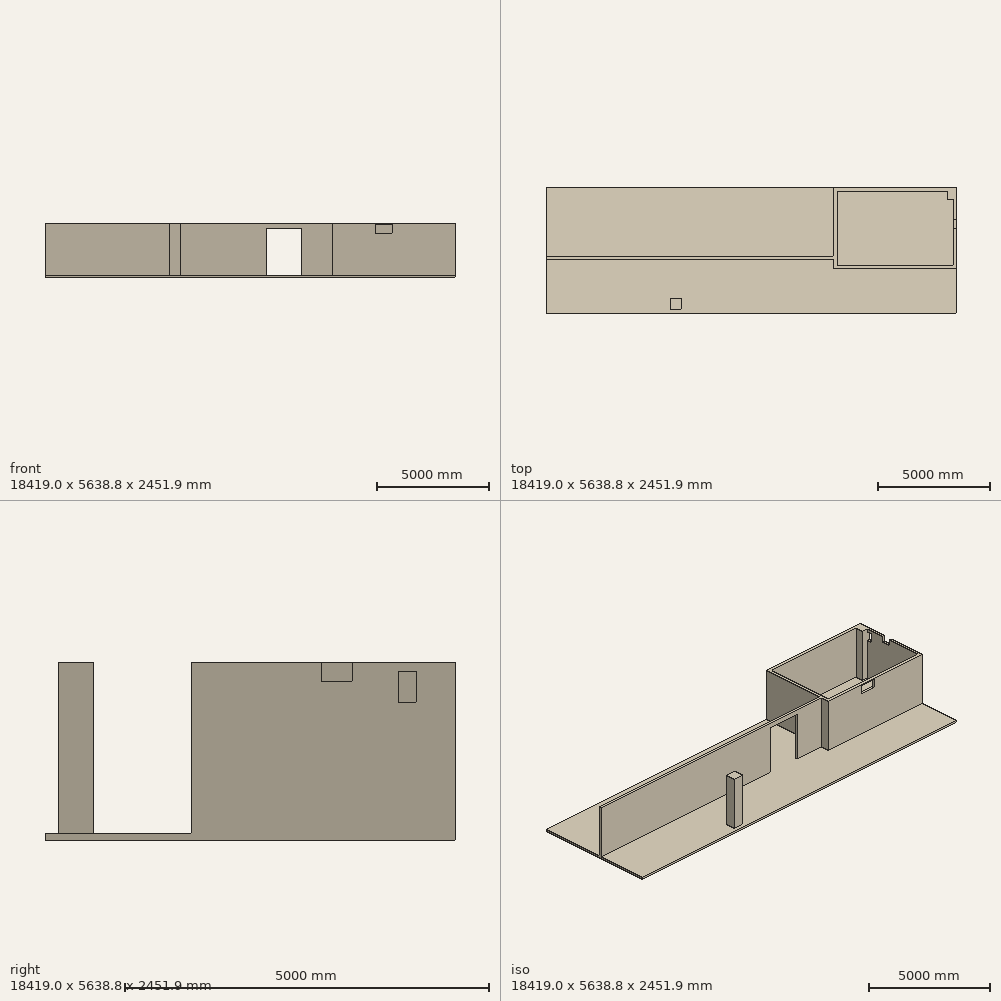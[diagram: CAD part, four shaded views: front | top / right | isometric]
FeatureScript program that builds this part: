
annotation { "Feature Type Name" : "Feature", "Feature Type Description" : "" }
export const myFeature = defineFeature(function(context is Context, id is Id, definition is map)
    precondition{}
    {
        {
            var Q0;
            Q0=qCreatedBy(makeId("Top.planeOp"),FACE);
            var sketch = newSketch(context, id + "F0", { "sketchPlane" : qUnion([Q0])});
            skLineSegment(sketch, "E0.bottom", {"start": v(0, 0) * mm, "end": v(18288, 0) * mm});
            skLineSegment(sketch, "E0.top", {"start": v(0, 5486.4) * mm, "end": v(18288, 5486.4) * mm});
            skLineSegment(sketch, "E0.left", {"start": v(0, 0) * mm, "end": v(0, 5486.4) * mm});
            skLineSegment(sketch, "E0.right", {"start": v(18288, 0) * mm, "end": v(18288, 5486.4) * mm});
            skSolve(sketch);
        }
        {
            var Q0;
            Q0=makeQuery(id+"F0.imprint","IMPRINT",FACE,{"disambiguationData":[TD([[makeQuery(id+"F0.imprint","IMPRINT",EDGE,{"derivedFrom":sQuery(id+"F0.wireOp",EDGE,"E0.bottom")}),1.0]])]});
            extrude(context, id + "F1", {"entities" : qUnion([Q0]), "depth" : 101.6 * mm});
        }
        {
            var Q0;
            Q0=makeQuery(id+"F1.opExtrude","CAP_FACE",FACE,{"disambiguationData":[OSD([sQuery(id+"F0.wireOp",EDGE,"E0.bottom"),sQuery(id+"F0.wireOp",EDGE,"E0.top"),sQuery(id+"F0.wireOp",EDGE,"E0.left"),sQuery(id+"F0.wireOp",EDGE,"E0.right")])],"isStart":false});
            var sketch = newSketch(context, id + "F2", { "sketchPlane" : qUnion([Q0])});
            skLineSegment(sketch, "E1.bottom", {"start": v(18288, 5486.4) * mm, "end": v(13335, 5486.4) * mm, "construction": true});
            skLineSegment(sketch, "E1.top", {"start": v(18288, 2128.84) * mm, "end": v(13335, 2128.84) * mm, "construction": true});
            skLineSegment(sketch, "E1.left", {"start": v(18288, 5486.4) * mm, "end": v(18288, 2128.84) * mm, "construction": true});
            skLineSegment(sketch, "E1.right", {"start": v(13335, 5486.4) * mm, "end": v(13335, 2128.84) * mm, "construction": true});
            skLineSegment(sketch, "E2.bottom", {"start": v(18288, 2128.84) * mm, "end": v(13335, 2128.84) * mm});
            skLineSegment(sketch, "E2.top", {"start": v(18288, 1976.44) * mm, "end": v(13335, 1976.44) * mm});
            skLineSegment(sketch, "E2.left", {"start": v(18288, 2128.84) * mm, "end": v(18288, 1976.44) * mm});
            skLineSegment(sketch, "E2.right", {"start": v(13335, 2128.84) * mm, "end": v(13335, 1976.44) * mm});
            skLineSegment(sketch, "E3.bottom", {"start": v(13335, 5486.4) * mm, "end": v(13182.6, 5486.4) * mm});
            skLineSegment(sketch, "E3.top", {"start": v(13335, 2128.84) * mm, "end": v(13182.6, 2128.84) * mm});
            skLineSegment(sketch, "E3.left", {"start": v(13335, 5486.4) * mm, "end": v(13335, 2128.84) * mm});
            skLineSegment(sketch, "E3.right", {"start": v(13182.6, 5486.4) * mm, "end": v(13182.6, 2128.84) * mm});
            skLineSegment(sketch, "E4.bottom", {"start": v(13335, 1976.44) * mm, "end": v(13182.6, 1976.44) * mm});
            skLineSegment(sketch, "E4.left", {"start": v(13335, 1976.44) * mm, "end": v(13335, 2128.84) * mm});
            skLineSegment(sketch, "E4.right", {"start": v(13182.6, 1976.44) * mm, "end": v(13182.6, 2128.84) * mm});
            skSolve(sketch);
        }
        {
            var Q0;
            Q0=makeQuery(id+"F2.imprint","IMPRINT",FACE,{"disambiguationData":[TD([[makeQuery(id+"F2.imprint","IMPRINT",EDGE,{"derivedFrom":sQuery(id+"F2.wireOp",EDGE,"E2.bottom")}),1.0]])]});
            var Q1;
            Q1=makeQuery(id+"F2.imprint","IMPRINT",FACE,{"disambiguationData":[TD([[makeQuery(id+"F2.imprint","IMPRINT",EDGE,{"derivedFrom":sQuery(id+"F2.wireOp",EDGE,"E3.bottom")}),-1.0]])]});
            var Q2;
            Q2=makeQuery(id+"F2.imprint","IMPRINT",FACE,{"disambiguationData":[TD([[makeQuery(id+"F2.imprint","IMPRINT",EDGE,{"derivedFrom":sQuery(id+"F2.wireOp",EDGE,"E4.bottom")}),-1.0]])]});
            extrude(context, id + "F3", {"entities" : qUnion([Q0, Q1, Q2]), "operationType" : NewBodyOperationType.ADD, "depth" : 2426.5 * mm});
        }
        {
            var Q0;
            Q0=makeQuery(id+"F3.boolean.opBoolean","MERGE",FACE,{"derivedFrom":[makeQuery(id+"F1.opExtrude","SWEPT_FACE",FACE,{"disambiguationData":[OSD([sQuery(id+"F0.wireOp",EDGE,"E0.right")])]}),makeQuery(id+"F3.opExtrude","SWEPT_FACE",FACE,{"disambiguationData":[OSD([sQuery(id+"F2.wireOp",EDGE,"E2.left")])]})]});
            extrude(context, id + "F4", {"entities" : qUnion([Q0]), "operationType" : NewBodyOperationType.ADD, "depth" : 152.4 * mm});
        }
        {
            var Q0;
            {var subQ0=sQuery(id+"F0.wireOp",EDGE,"E0.top");Q0=makeQuery(id+"F4.boolean.opBoolean","MERGE",FACE,{"derivedFrom":[makeQuery(id+"F3.boolean.opBoolean","MERGE",FACE,{"derivedFrom":[makeQuery(id+"F1.opExtrude","SWEPT_FACE",FACE,{"disambiguationData":[OSD([subQ0])]}),makeQuery(id+"F3.opExtrude","SWEPT_FACE",FACE,{"disambiguationData":[OSD([sQuery(id+"F2.wireOp",EDGE,"E3.bottom")])]})]}),makeQuery(id+"F4.opExtrude","SWEPT_FACE",FACE,{"disambiguationData":[OSD([subQ0,sQuery(id+"F0.wireOp",EDGE,"E0.right")])]})]});}
            extrude(context, id + "F5", {"entities" : qUnion([Q0]), "operationType" : NewBodyOperationType.ADD, "depth" : 152.4 * mm});
        }
        {
            var Q0;
            {var subQ0=sQuery(id+"F0.wireOp",EDGE,"E0.right");var subQ1=sQuery(id+"F0.wireOp",EDGE,"E0.top");var subQ3=makeQuery(id+"F1.opExtrude","SWEPT_FACE",FACE,{"disambiguationData":[OSD([subQ0])]});var subQ4=makeQuery(id+"F1.opExtrude","SWEPT_FACE",FACE,{"disambiguationData":[OSD([subQ1])]});var subQ5=makeQuery(id+"F1.opExtrude","CAP_FACE",FACE,{"disambiguationData":[OSD([sQuery(id+"F0.wireOp",EDGE,"E0.bottom"),subQ1,sQuery(id+"F0.wireOp",EDGE,"E0.left"),subQ0])],"isStart":false});var subQ8=makeQuery(id+"F3.opExtrude","SWEPT_FACE",FACE,{"disambiguationData":[OSD([sQuery(id+"F2.wireOp",EDGE,"E2.bottom")])]});Q0=makeQuery(id+"F5.boolean.opBoolean","MERGE",FACE,{"derivedFrom":[makeQuery(id+"F4.boolean.opBoolean","MERGE",FACE,{"derivedFrom":[makeQuery(id+"F3.boolean.opBoolean","SPLIT",FACE,{"disambiguationData":[TD([subQ8])],"derivedFrom":subQ5}),makeQuery(id+"F4.opExtrude","SWEPT_FACE",FACE,{"disambiguationData":[OSD([subQ0]),TDD([makeQuery(id+"F3.boolean.opBoolean","SPLIT",EDGE,{"disambiguationData":[TD([subQ4])],"derivedFrom":makeQuery(id+"F1.opExtrude","CAP_EDGE",EDGE,{"disambiguationData":[OSD([subQ0])],"isStart":false})})])]})]}),makeQuery(id+"F5.opExtrude","SWEPT_FACE",FACE,{"disambiguationData":[OSD([subQ1,subQ0]),TDD([makeQuery(id+"F4.boolean.opBoolean","MERGE",EDGE,{"derivedFrom":[makeQuery(id+"F3.boolean.opBoolean","SPLIT",EDGE,{"disambiguationData":[TD([subQ3])],"derivedFrom":makeQuery(id+"F1.opExtrude","CAP_EDGE",EDGE,{"disambiguationData":[OSD([subQ1])],"isStart":false})}),makeQuery(id+"F4.opExtrude","SWEPT_EDGE",EDGE,{"disambiguationData":[OSD([subQ1,subQ0]),TDD([makeQuery(id+"F1.opExtrude","CAP_VERTEX",VERTEX,{"disambiguationData":[OSD([subQ1,subQ0])],"isStart":false})])]})]})])]})]});}
            var sketch = newSketch(context, id + "F6", { "sketchPlane" : qUnion([Q0])});
            skLineSegment(sketch, "E5.bottom", {"start": v(18440.4, 2128.84) * mm, "end": v(18288, 2128.84) * mm});
            skLineSegment(sketch, "E5.top", {"start": v(18440.4, 5638.8) * mm, "end": v(18288, 5638.8) * mm});
            skLineSegment(sketch, "E5.left", {"start": v(18440.4, 2128.84) * mm, "end": v(18440.4, 5638.8) * mm});
            skLineSegment(sketch, "E5.right", {"start": v(18288, 2128.84) * mm, "end": v(18288, 5638.8) * mm});
            skLineSegment(sketch, "E6.bottom", {"start": v(13335, 5638.8) * mm, "end": v(18288, 5638.8) * mm});
            skLineSegment(sketch, "E6.top", {"start": v(13335, 5486.4) * mm, "end": v(18288, 5486.4) * mm});
            skLineSegment(sketch, "E6.left", {"start": v(13335, 5638.8) * mm, "end": v(13335, 5486.4) * mm});
            skLineSegment(sketch, "E6.right", {"start": v(18288, 5638.8) * mm, "end": v(18288, 5486.4) * mm});
            skSolve(sketch);
        }
        {
            var Q0;
            Q0=makeQuery(id+"F6.imprint","IMPRINT",FACE,{"disambiguationData":[TD([[makeQuery(id+"F6.imprint","IMPRINT",EDGE,{"derivedFrom":sQuery(id+"F6.wireOp",EDGE,"E6.bottom")}),-1.0]])]});
            var Q1;
            Q1=makeQuery(id+"F6.imprint","IMPRINT",FACE,{"disambiguationData":[TD([[makeQuery(id+"F6.imprint","IMPRINT",EDGE,{"derivedFrom":sQuery(id+"F6.wireOp",EDGE,"E5.bottom")}),-1.0]])]});
            extrude(context, id + "F7", {"entities" : qUnion([Q0, Q1]), "operationType" : NewBodyOperationType.ADD, "depth" : 2350.3 * mm});
        }
        {
            var Q0;
            {var subQ0=sQuery(id+"F2.wireOp",EDGE,"E3.bottom");var subQ1=sQuery(id+"F2.wireOp",EDGE,"E2.left");Q0=makeQuery(id+"F5.boolean.opBoolean","MERGE",FACE,{"derivedFrom":[makeQuery(id+"F4.boolean.opBoolean","MERGE",FACE,{"derivedFrom":[makeQuery(id+"F3.opExtrude","CAP_FACE",FACE,{"disambiguationData":[OSD([sQuery(id+"F2.wireOp",EDGE,"E2.bottom"),sQuery(id+"F2.wireOp",EDGE,"E2.top"),subQ1,subQ0,sQuery(id+"F2.wireOp",EDGE,"E3.left"),sQuery(id+"F2.wireOp",EDGE,"E3.right"),sQuery(id+"F2.wireOp",EDGE,"E4.bottom"),sQuery(id+"F2.wireOp",EDGE,"E4.right")])],"isStart":false}),makeQuery(id+"F4.opExtrude","SWEPT_FACE",FACE,{"disambiguationData":[OSD([subQ1])]})]}),makeQuery(id+"F5.opExtrude","SWEPT_FACE",FACE,{"disambiguationData":[OSD([subQ0])]})]});}
            extrude(context, id + "F8", {"entities" : qUnion([Q0]), "operationType" : NewBodyOperationType.REMOVE, "oppositeDirection" : true, "depth" : 76.2 * mm});
        }
        {
            var Q0;
            {var subQ0=sQuery(id+"F0.wireOp",EDGE,"E0.right");var subQ1=sQuery(id+"F0.wireOp",EDGE,"E0.top");var subQ3=makeQuery(id+"F1.opExtrude","SWEPT_FACE",FACE,{"disambiguationData":[OSD([subQ0])]});var subQ4=makeQuery(id+"F1.opExtrude","SWEPT_FACE",FACE,{"disambiguationData":[OSD([subQ1])]});var subQ5=makeQuery(id+"F1.opExtrude","CAP_FACE",FACE,{"disambiguationData":[OSD([sQuery(id+"F0.wireOp",EDGE,"E0.bottom"),subQ1,sQuery(id+"F0.wireOp",EDGE,"E0.left"),subQ0])],"isStart":false});var subQ8=makeQuery(id+"F3.opExtrude","SWEPT_FACE",FACE,{"disambiguationData":[OSD([sQuery(id+"F2.wireOp",EDGE,"E2.bottom")])]});Q0=makeQuery(id+"F5.boolean.opBoolean","MERGE",FACE,{"derivedFrom":[makeQuery(id+"F4.boolean.opBoolean","MERGE",FACE,{"derivedFrom":[makeQuery(id+"F3.boolean.opBoolean","SPLIT",FACE,{"disambiguationData":[TD([subQ8])],"derivedFrom":subQ5}),makeQuery(id+"F4.opExtrude","SWEPT_FACE",FACE,{"disambiguationData":[OSD([subQ0]),TDD([makeQuery(id+"F3.boolean.opBoolean","SPLIT",EDGE,{"disambiguationData":[TD([subQ4])],"derivedFrom":makeQuery(id+"F1.opExtrude","CAP_EDGE",EDGE,{"disambiguationData":[OSD([subQ0])],"isStart":false})})])]})]}),makeQuery(id+"F5.opExtrude","SWEPT_FACE",FACE,{"disambiguationData":[OSD([subQ1,subQ0]),TDD([makeQuery(id+"F4.boolean.opBoolean","MERGE",EDGE,{"derivedFrom":[makeQuery(id+"F3.boolean.opBoolean","SPLIT",EDGE,{"disambiguationData":[TD([subQ3])],"derivedFrom":makeQuery(id+"F1.opExtrude","CAP_EDGE",EDGE,{"disambiguationData":[OSD([subQ1])],"isStart":false})}),makeQuery(id+"F4.opExtrude","SWEPT_EDGE",EDGE,{"disambiguationData":[OSD([subQ1,subQ0]),TDD([makeQuery(id+"F1.opExtrude","CAP_VERTEX",VERTEX,{"disambiguationData":[OSD([subQ1,subQ0])],"isStart":false})])]})]})])]})]});}
            var sketch = newSketch(context, id + "F9", { "sketchPlane" : qUnion([Q0])});
            skLineSegment(sketch, "E7.bottom", {"start": v(18288, 5486.4) * mm, "end": v(17907, 5486.4) * mm});
            skLineSegment(sketch, "E7.top", {"start": v(18288, 5207) * mm, "end": v(17907, 5207) * mm});
            skLineSegment(sketch, "E7.left", {"start": v(18288, 5486.4) * mm, "end": v(18288, 5207) * mm});
            skLineSegment(sketch, "E7.right", {"start": v(17907, 5486.4) * mm, "end": v(17907, 5207) * mm});
            skSolve(sketch);
        }
        {
            var Q0;
            Q0=makeQuery(id+"F9.imprint","IMPRINT",FACE,{"disambiguationData":[TD([[makeQuery(id+"F9.imprint","IMPRINT",EDGE,{"derivedFrom":sQuery(id+"F9.wireOp",EDGE,"E7.bottom")}),-1.0]])]});
            var Q1;
            Q1=makeQuery(id+"F8.boolean.opBoolean","MERGE",FACE,{"derivedFrom":[makeQuery(id+"F7.opExtrude","CAP_FACE",FACE,{"disambiguationData":[OSD([sQuery(id+"F6.wireOp",EDGE,"E5.bottom"),sQuery(id+"F6.wireOp",EDGE,"E5.top"),sQuery(id+"F6.wireOp",EDGE,"E5.left"),sQuery(id+"F6.wireOp",EDGE,"E5.right"),sQuery(id+"F6.wireOp",EDGE,"E6.bottom"),sQuery(id+"F6.wireOp",EDGE,"E6.top"),sQuery(id+"F6.wireOp",EDGE,"E6.left")])],"isStart":false}),makeQuery(id+"F8.opExtrude","CAP_FACE",FACE,{"disambiguationData":[OSD([sQuery(id+"F2.wireOp",EDGE,"E2.bottom"),sQuery(id+"F2.wireOp",EDGE,"E2.top"),sQuery(id+"F2.wireOp",EDGE,"E2.left"),sQuery(id+"F2.wireOp",EDGE,"E3.bottom"),sQuery(id+"F2.wireOp",EDGE,"E3.left"),sQuery(id+"F2.wireOp",EDGE,"E3.right"),sQuery(id+"F2.wireOp",EDGE,"E4.bottom"),sQuery(id+"F2.wireOp",EDGE,"E4.right")])],"isStart":false})]});
            extrude(context, id + "F10", {"entities" : qUnion([Q0]), "operationType" : NewBodyOperationType.ADD, "endBound" : BoundingType.UP_TO_SURFACE, "endBoundEntityFace" : qUnion([Q1]), "depth" : 25.4 * mm});
        }
        {
            var Q0;
            Q0=makeQuery(id+"F10.opExtrude","SWEPT_FACE",FACE,{"disambiguationData":[OSD([sQuery(id+"F9.wireOp",EDGE,"E7.top")])]});
            extrude(context, id + "F11", {"entities" : qUnion([Q0]), "operationType" : NewBodyOperationType.ADD, "depth" : 101.6 * mm});
        }
        {
            var Q0;
            {var subQ0=sQuery(id+"F9.wireOp",EDGE,"E7.right");Q0=makeQuery(id+"F11.boolean.opBoolean","MERGE",FACE,{"derivedFrom":[makeQuery(id+"F10.opExtrude","SWEPT_FACE",FACE,{"disambiguationData":[OSD([subQ0])]}),makeQuery(id+"F11.opExtrude","SWEPT_FACE",FACE,{"disambiguationData":[OSD([sQuery(id+"F9.wireOp",EDGE,"E7.top"),subQ0])]})]});}
            extrude(context, id + "F12", {"entities" : qUnion([Q0]), "operationType" : NewBodyOperationType.REMOVE, "oppositeDirection" : true, "depth" : 101.6 * mm});
        }
        {
            var Q0;
            {var subQ0=sQuery(id+"F2.wireOp",EDGE,"E3.right");Q0=makeQuery(id+"F5.boolean.opBoolean","MERGE",FACE,{"derivedFrom":[makeQuery(id+"F3.opExtrude","SWEPT_FACE",FACE,{"disambiguationData":[OSD([subQ0,sQuery(id+"F2.wireOp",EDGE,"E4.right")])]}),makeQuery(id+"F5.opExtrude","SWEPT_FACE",FACE,{"disambiguationData":[OSD([sQuery(id+"F0.wireOp",EDGE,"E0.top"),sQuery(id+"F2.wireOp",EDGE,"E3.bottom"),subQ0])]})]});}
            extrude(context, id + "F13", {"entities" : qUnion([Q0]), "operationType" : NewBodyOperationType.ADD, "depth" : 275.43 * mm});
        }
        {
            var Q0;
            {var subQ0=sQuery(id+"F2.wireOp",EDGE,"E3.left");Q0=makeQuery(id+"F5.boolean.opBoolean","MERGE",FACE,{"derivedFrom":[makeQuery(id+"F3.opExtrude","SWEPT_FACE",FACE,{"disambiguationData":[OSD([subQ0])]}),makeQuery(id+"F5.opExtrude","SWEPT_FACE",FACE,{"disambiguationData":[OSD([sQuery(id+"F0.wireOp",EDGE,"E0.top"),sQuery(id+"F2.wireOp",EDGE,"E3.bottom"),subQ0])]})]});}
            extrude(context, id + "F14", {"entities" : qUnion([Q0]), "operationType" : NewBodyOperationType.REMOVE, "oppositeDirection" : true, "depth" : 275.43 * mm});
        }
        {
            var Q0;
            {var subQ0=sQuery(id+"F2.wireOp",EDGE,"E4.bottom");var subQ1=sQuery(id+"F2.wireOp",EDGE,"E2.top");Q0=makeQuery(id+"F13.boolean.opBoolean","MERGE",FACE,{"derivedFrom":[makeQuery(id+"F4.boolean.opBoolean","MERGE",FACE,{"derivedFrom":[makeQuery(id+"F3.opExtrude","SWEPT_FACE",FACE,{"disambiguationData":[OSD([subQ1,subQ0])]}),makeQuery(id+"F4.opExtrude","SWEPT_FACE",FACE,{"disambiguationData":[OSD([sQuery(id+"F0.wireOp",EDGE,"E0.right"),subQ1,sQuery(id+"F2.wireOp",EDGE,"E2.left")])]})]}),makeQuery(id+"F13.opExtrude","SWEPT_FACE",FACE,{"disambiguationData":[OSD([subQ0,sQuery(id+"F2.wireOp",EDGE,"E4.right")])]})]});}
            extrude(context, id + "F15", {"entities" : qUnion([Q0]), "operationType" : NewBodyOperationType.REMOVE, "oppositeDirection" : true, "depth" : 25.4 * mm});
        }
        {
            var Q0;
            {var subQ0=sQuery(id+"F2.wireOp",EDGE,"E2.bottom");Q0=makeQuery(id+"F14.boolean.opBoolean","MERGE",FACE,{"derivedFrom":[makeQuery(id+"F4.boolean.opBoolean","MERGE",FACE,{"derivedFrom":[makeQuery(id+"F3.opExtrude","SWEPT_FACE",FACE,{"disambiguationData":[OSD([subQ0])]}),makeQuery(id+"F4.opExtrude","SWEPT_FACE",FACE,{"disambiguationData":[OSD([sQuery(id+"F0.wireOp",EDGE,"E0.right"),subQ0,sQuery(id+"F2.wireOp",EDGE,"E2.left")])]})]}),makeQuery(id+"F14.opExtrude","SWEPT_FACE",FACE,{"disambiguationData":[OSD([subQ0,sQuery(id+"F2.wireOp",EDGE,"E3.left"),sQuery(id+"F2.wireOp",EDGE,"E3.top"),sQuery(id+"F2.wireOp",EDGE,"E4.left")])]})]});}
            var sketch = newSketch(context, id + "F16", { "sketchPlane" : qUnion([Q0])});
            skLineSegment(sketch, "E8.bottom", {"start": v(-13059.57, 2451.9) * mm, "end": v(-14431.17, 2451.9) * mm, "construction": true});
            skLineSegment(sketch, "E8.top", {"start": v(-13059.57, 2197.9) * mm, "end": v(-14431.17, 2197.9) * mm, "construction": true});
            skLineSegment(sketch, "E8.left", {"start": v(-13059.57, 2451.9) * mm, "end": v(-13059.57, 2197.9) * mm, "construction": true});
            skLineSegment(sketch, "E8.right", {"start": v(-14431.17, 2451.9) * mm, "end": v(-14431.17, 2197.9) * mm, "construction": true});
            skLineSegment(sketch, "E9.bottom", {"start": v(-14431.17, 2197.9) * mm, "end": v(-15193.17, 2197.9) * mm});
            skLineSegment(sketch, "E9.top", {"start": v(-14431.17, 1943.9) * mm, "end": v(-15193.17, 1943.9) * mm});
            skLineSegment(sketch, "E9.left", {"start": v(-14431.17, 2197.9) * mm, "end": v(-14431.17, 1943.9) * mm});
            skLineSegment(sketch, "E9.right", {"start": v(-15193.17, 2197.9) * mm, "end": v(-15193.17, 1943.9) * mm});
            skSolve(sketch);
        }
        {
            var Q0;
            Q0=makeQuery(id+"F16.imprint","IMPRINT",FACE,{"disambiguationData":[TD([[makeQuery(id+"F16.imprint","IMPRINT",EDGE,{"derivedFrom":sQuery(id+"F16.wireOp",EDGE,"E9.bottom")}),1.0]])]});
            extrude(context, id + "F17", {"entities" : qUnion([Q0]), "operationType" : NewBodyOperationType.REMOVE, "endBound" : BoundingType.THROUGH_ALL, "oppositeDirection" : true, "depth" : 25.4 * mm});
        }
        {
            var Q0;
            Q0=makeQuery(id+"F17.boolean.opBoolean","COPY",FACE,{"derivedFrom":makeQuery(id+"F17.opExtrude","SWEPT_FACE",FACE,{"disambiguationData":[OSD([sQuery(id+"F16.wireOp",EDGE,"E9.bottom")])]})});
            extrude(context, id + "F18", {"entities" : qUnion([Q0]), "operationType" : NewBodyOperationType.REMOVE, "oppositeDirection" : true, "depth" : 190.5 * mm});
        }
        {
            var Q0;
            Q0=makeQuery(id+"F17.boolean.opBoolean","COPY",FACE,{"derivedFrom":makeQuery(id+"F17.opExtrude","SWEPT_FACE",FACE,{"disambiguationData":[OSD([sQuery(id+"F16.wireOp",EDGE,"E9.top")])]})});
            extrude(context, id + "F19", {"entities" : qUnion([Q0]), "operationType" : NewBodyOperationType.ADD, "depth" : 63.5 * mm});
        }
        {
            var Q0;
            Q0=makeQuery(id+"F7.opExtrude","SWEPT_FACE",FACE,{"disambiguationData":[OSD([sQuery(id+"F6.wireOp",EDGE,"E5.right")])]});
            var sketch = newSketch(context, id + "F20", { "sketchPlane" : qUnion([Q0])});
            skLineSegment(sketch, "E10.bottom", {"start": v(-5105.4, 2451.9) * mm, "end": v(-4851.4, 2451.9) * mm, "construction": true});
            skLineSegment(sketch, "E10.top", {"start": v(-5105.4, 2375.7) * mm, "end": v(-4851.4, 2375.7) * mm, "construction": true});
            skLineSegment(sketch, "E10.left", {"start": v(-5105.4, 2451.9) * mm, "end": v(-5105.4, 2375.7) * mm, "construction": true});
            skLineSegment(sketch, "E10.right", {"start": v(-4851.4, 2451.9) * mm, "end": v(-4851.4, 2375.7) * mm, "construction": true});
            skLineSegment(sketch, "E11.bottom", {"start": v(-4851.4, 2375.7) * mm, "end": v(-5105.4, 2375.7) * mm});
            skLineSegment(sketch, "E11.top", {"start": v(-4851.4, 2070.9) * mm, "end": v(-5105.4, 2070.9) * mm});
            skLineSegment(sketch, "E11.left", {"start": v(-4851.4, 2375.7) * mm, "end": v(-4851.4, 2070.9) * mm});
            skLineSegment(sketch, "E11.right", {"start": v(-5105.4, 2375.7) * mm, "end": v(-5105.4, 2070.9) * mm});
            skSolve(sketch);
        }
        {
            var Q0;
            Q0=makeQuery(id+"F20.imprint","IMPRINT",FACE,{"disambiguationData":[TD([[makeQuery(id+"F20.imprint","IMPRINT",EDGE,{"derivedFrom":sQuery(id+"F20.wireOp",EDGE,"E11.bottom")}),1.0]])]});
            extrude(context, id + "F21", {"entities" : qUnion([Q0]), "operationType" : NewBodyOperationType.REMOVE, "endBound" : BoundingType.THROUGH_ALL, "oppositeDirection" : true, "depth" : 25.4 * mm});
        }
        {
            var Q0;
            Q0=makeQuery(id+"F7.opExtrude","SWEPT_FACE",FACE,{"disambiguationData":[OSD([sQuery(id+"F6.wireOp",EDGE,"E5.right")])]});
            var sketch = newSketch(context, id + "F22", { "sketchPlane" : qUnion([Q0])});
            skLineSegment(sketch, "E12.bottom", {"start": v(-4851.4, 2375.7) * mm, "end": v(-3606.8, 2375.7) * mm, "construction": true});
            skLineSegment(sketch, "E12.top", {"start": v(-4851.4, 2070.9) * mm, "end": v(-3606.8, 2070.9) * mm, "construction": true});
            skLineSegment(sketch, "E12.left", {"start": v(-4851.4, 2375.7) * mm, "end": v(-4851.4, 2070.9) * mm, "construction": true});
            skLineSegment(sketch, "E12.right", {"start": v(-3606.8, 2375.7) * mm, "end": v(-3606.8, 2070.9) * mm, "construction": true});
            skLineSegment(sketch, "E13.bottom", {"start": v(-3606.8, 2375.7) * mm, "end": v(-3888.54, 2375.7) * mm});
            skLineSegment(sketch, "E13.top", {"start": v(-3606.8, 2070.9) * mm, "end": v(-3888.54, 2070.9) * mm});
            skLineSegment(sketch, "E13.left", {"start": v(-3606.8, 2375.7) * mm, "end": v(-3606.8, 2070.9) * mm});
            skLineSegment(sketch, "E13.right", {"start": v(-3888.54, 2375.7) * mm, "end": v(-3888.54, 2070.9) * mm});
            skSolve(sketch);
        }
        {
            var Q0;
            Q0=makeQuery(id+"F22.imprint","IMPRINT",FACE,{"disambiguationData":[TD([[makeQuery(id+"F22.imprint","IMPRINT",EDGE,{"derivedFrom":sQuery(id+"F22.wireOp",EDGE,"E13.bottom")}),1.0]])]});
            extrude(context, id + "F23", {"entities" : qUnion([Q0]), "operationType" : NewBodyOperationType.REMOVE, "endBound" : BoundingType.THROUGH_ALL, "oppositeDirection" : true, "depth" : 25.4 * mm});
        }
        {
            var Q0;
            Q0=makeQuery(id+"F23.boolean.opBoolean","COPY",FACE,{"derivedFrom":makeQuery(id+"F23.opExtrude","SWEPT_FACE",FACE,{"disambiguationData":[OSD([sQuery(id+"F22.wireOp",EDGE,"E13.right")])]})});
            extrude(context, id + "F24", {"entities" : qUnion([Q0]), "operationType" : NewBodyOperationType.REMOVE, "oppositeDirection" : true, "depth" : 304.8 * mm});
        }
        {
            var Q0;
            Q0=makeQuery(id+"F23.boolean.opBoolean","COPY",FACE,{"derivedFrom":makeQuery(id+"F23.opExtrude","SWEPT_FACE",FACE,{"disambiguationData":[OSD([sQuery(id+"F22.wireOp",EDGE,"E13.left")])]})});
            extrude(context, id + "F25", {"entities" : qUnion([Q0]), "operationType" : NewBodyOperationType.ADD, "depth" : 304.8 * mm});
        }
        {
            var Q0;
            Q0=makeQuery(id+"F24.boolean.opBoolean","COPY",FACE,{"derivedFrom":makeQuery(id+"F24.opExtrude","CAP_FACE",FACE,{"disambiguationData":[OSD([sQuery(id+"F22.wireOp",EDGE,"E13.right")])],"isStart":false})});
            extrude(context, id + "F26", {"entities" : qUnion([Q0]), "operationType" : NewBodyOperationType.ADD, "depth" : 25.4 * mm});
        }
        {
            var Q0;
            Q0=makeQuery(id+"F25.opExtrude","CAP_FACE",FACE,{"disambiguationData":[OSD([sQuery(id+"F22.wireOp",EDGE,"E13.left")])],"isStart":false});
            extrude(context, id + "F27", {"entities" : qUnion([Q0]), "operationType" : NewBodyOperationType.REMOVE, "oppositeDirection" : true, "depth" : 25.4 * mm});
        }
        {
            var Q0;
            Q0=makeQuery(id+"F27.boolean.opBoolean","COPY",FACE,{"derivedFrom":makeQuery(id+"F27.opExtrude","CAP_FACE",FACE,{"disambiguationData":[OSD([sQuery(id+"F22.wireOp",EDGE,"E13.left")])],"isStart":false})});
            extrude(context, id + "F28", {"entities" : qUnion([Q0]), "operationType" : NewBodyOperationType.REMOVE, "oppositeDirection" : true, "depth" : 12.7 * mm});
        }
        {
            var Q0;
            Q0=makeQuery(id+"F26.opExtrude","CAP_FACE",FACE,{"disambiguationData":[OSD([sQuery(id+"F22.wireOp",EDGE,"E13.right")])],"isStart":false});
            extrude(context, id + "F29", {"entities" : qUnion([Q0]), "operationType" : NewBodyOperationType.ADD, "depth" : 12.7 * mm});
        }
        {
            var Q0;
            Q0=makeQuery(id+"F13.opExtrude","CAP_FACE",FACE,{"disambiguationData":[OSD([sQuery(id+"F0.wireOp",EDGE,"E0.top"),sQuery(id+"F2.wireOp",EDGE,"E3.bottom"),sQuery(id+"F2.wireOp",EDGE,"E3.right"),sQuery(id+"F2.wireOp",EDGE,"E4.right")])],"isStart":false});
            var sketch = newSketch(context, id + "F30", { "sketchPlane" : qUnion([Q0])});
            skLineSegment(sketch, "E14.bottom", {"start": v(-2001.84, 2451.9) * mm, "end": v(-2408.24, 2451.9) * mm, "construction": true});
            skLineSegment(sketch, "E14.top", {"start": v(-2001.84, 1527.67) * mm, "end": v(-2408.24, 1527.67) * mm, "construction": true});
            skLineSegment(sketch, "E14.left", {"start": v(-2001.84, 2451.9) * mm, "end": v(-2001.84, 1527.67) * mm, "construction": true});
            skLineSegment(sketch, "E14.right", {"start": v(-2408.24, 2451.9) * mm, "end": v(-2408.24, 1527.67) * mm, "construction": true});
            skLineSegment(sketch, "E15.bottom", {"start": v(-2408.24, 2451.9) * mm, "end": v(-2535.24, 2451.9) * mm});
            skLineSegment(sketch, "E15.top", {"start": v(-2408.24, 101.6) * mm, "end": v(-2535.24, 101.6) * mm});
            skLineSegment(sketch, "E15.left", {"start": v(-2408.24, 2451.9) * mm, "end": v(-2408.24, 101.6) * mm});
            skLineSegment(sketch, "E15.right", {"start": v(-2535.24, 2451.9) * mm, "end": v(-2535.24, 101.6) * mm});
            skSolve(sketch);
        }
        {
            var Q0;
            Q0=makeQuery(id+"F30.imprint","IMPRINT",FACE,{"disambiguationData":[TD([[makeQuery(id+"F30.imprint","IMPRINT",EDGE,{"derivedFrom":sQuery(id+"F30.wireOp",EDGE,"E15.bottom")}),-1.0]])]});
            var Q1;
            {var subQ0=sQuery(id+"F0.wireOp",EDGE,"E0.left");Q1=makeQuery(id+"F5.boolean.opBoolean","MERGE",FACE,{"derivedFrom":[makeQuery(id+"F1.opExtrude","SWEPT_FACE",FACE,{"disambiguationData":[OSD([subQ0])]}),makeQuery(id+"F5.opExtrude","SWEPT_FACE",FACE,{"disambiguationData":[OSD([sQuery(id+"F0.wireOp",EDGE,"E0.top"),subQ0])]})]});}
            extrude(context, id + "F31", {"entities" : qUnion([Q0]), "operationType" : NewBodyOperationType.ADD, "endBound" : BoundingType.UP_TO_SURFACE, "endBoundEntityFace" : qUnion([Q1]), "depth" : 25.4 * mm});
        }
        {
            var Q0;
            Q0=makeQuery(id+"F31.opExtrude","SWEPT_FACE",FACE,{"disambiguationData":[OSD([sQuery(id+"F30.wireOp",EDGE,"E15.left")])]});
            var sketch = newSketch(context, id + "F32", { "sketchPlane" : qUnion([Q0])});
            skLineSegment(sketch, "E16.bottom", {"start": v(12907.17, 101.6) * mm, "end": v(12805.57, 101.6) * mm, "construction": true});
            skLineSegment(sketch, "E16.top", {"start": v(12907.17, 469.78) * mm, "end": v(12805.57, 469.78) * mm, "construction": true});
            skLineSegment(sketch, "E16.left", {"start": v(12907.17, 101.6) * mm, "end": v(12907.17, 469.78) * mm, "construction": true});
            skLineSegment(sketch, "E16.right", {"start": v(12805.57, 101.6) * mm, "end": v(12805.57, 469.78) * mm, "construction": true});
            skLineSegment(sketch, "E17.bottom", {"start": v(12805.57, 101.6) * mm, "end": v(11230.77, 101.6) * mm});
            skLineSegment(sketch, "E17.top", {"start": v(12805.57, 2235.2) * mm, "end": v(11230.77, 2235.2) * mm});
            skLineSegment(sketch, "E17.left", {"start": v(12805.57, 101.6) * mm, "end": v(12805.57, 2235.2) * mm});
            skLineSegment(sketch, "E17.right", {"start": v(11230.77, 101.6) * mm, "end": v(11230.77, 2235.2) * mm});
            skSolve(sketch);
        }
        {
            var Q0;
            Q0=makeQuery(id+"F32.imprint","IMPRINT",FACE,{"disambiguationData":[TD([[makeQuery(id+"F32.imprint","IMPRINT",EDGE,{"derivedFrom":sQuery(id+"F32.wireOp",EDGE,"E17.bottom")}),1.0]])]});
            extrude(context, id + "F33", {"entities" : qUnion([Q0]), "operationType" : NewBodyOperationType.REMOVE, "endBound" : BoundingType.THROUGH_ALL, "oppositeDirection" : true, "depth" : 25.4 * mm});
        }
        {
            var Q0;
            Q0=makeQuery(id+"F33.boolean.opBoolean","COPY",FACE,{"derivedFrom":makeQuery(id+"F33.opExtrude","SWEPT_FACE",FACE,{"disambiguationData":[OSD([sQuery(id+"F32.wireOp",EDGE,"E17.right")])]})});
            extrude(context, id + "F34", {"entities" : qUnion([Q0]), "operationType" : NewBodyOperationType.REMOVE, "oppositeDirection" : true, "depth" : 1320.8 * mm});
        }
        {
            var Q0;
            Q0=makeQuery(id+"F33.boolean.opBoolean","COPY",FACE,{"derivedFrom":makeQuery(id+"F33.opExtrude","SWEPT_FACE",FACE,{"disambiguationData":[OSD([sQuery(id+"F32.wireOp",EDGE,"E17.left")])]})});
            extrude(context, id + "F35", {"entities" : qUnion([Q0]), "operationType" : NewBodyOperationType.ADD, "depth" : 1320.8 * mm});
        }
        {
            var Q0;
            {var subQ0=sQuery(id+"F22.wireOp",EDGE,"E13.left");var subQ1=sQuery(id+"F22.wireOp",EDGE,"E13.top");Q0=makeQuery(id+"F28.boolean.opBoolean","MERGE",FACE,{"derivedFrom":[makeQuery(id+"F27.boolean.opBoolean","MERGE",FACE,{"derivedFrom":[makeQuery(id+"F24.boolean.opBoolean","MERGE",FACE,{"derivedFrom":[makeQuery(id+"F23.boolean.opBoolean","COPY",FACE,{"derivedFrom":makeQuery(id+"F23.opExtrude","SWEPT_FACE",FACE,{"disambiguationData":[OSD([subQ1])]})}),makeQuery(id+"F24.opExtrude","SWEPT_FACE",FACE,{"disambiguationData":[OSD([subQ1,sQuery(id+"F22.wireOp",EDGE,"E13.right")])]})]}),makeQuery(id+"F27.opExtrude","SWEPT_FACE",FACE,{"disambiguationData":[OSD([subQ1,subQ0])]})]}),makeQuery(id+"F28.opExtrude","SWEPT_FACE",FACE,{"disambiguationData":[OSD([subQ1,subQ0])]})]});}
            extrude(context, id + "F36", {"entities" : qUnion([Q0]), "operationType" : NewBodyOperationType.ADD, "depth" : 120.65 * mm});
        }
        {
            var Q0;
            {var subQ0=sQuery(id+"F22.wireOp",EDGE,"E13.left");var subQ1=sQuery(id+"F22.wireOp",EDGE,"E13.bottom");Q0=makeQuery(id+"F28.boolean.opBoolean","MERGE",FACE,{"derivedFrom":[makeQuery(id+"F27.boolean.opBoolean","MERGE",FACE,{"derivedFrom":[makeQuery(id+"F24.boolean.opBoolean","MERGE",FACE,{"derivedFrom":[makeQuery(id+"F23.boolean.opBoolean","COPY",FACE,{"derivedFrom":makeQuery(id+"F23.opExtrude","SWEPT_FACE",FACE,{"disambiguationData":[OSD([subQ1])]})}),makeQuery(id+"F24.opExtrude","SWEPT_FACE",FACE,{"disambiguationData":[OSD([subQ1,sQuery(id+"F22.wireOp",EDGE,"E13.right")])]})]}),makeQuery(id+"F27.opExtrude","SWEPT_FACE",FACE,{"disambiguationData":[OSD([subQ1,subQ0])]})]}),makeQuery(id+"F28.opExtrude","SWEPT_FACE",FACE,{"disambiguationData":[OSD([subQ1,subQ0])]})]});}
            extrude(context, id + "F37", {"entities" : qUnion([Q0]), "operationType" : NewBodyOperationType.REMOVE, "endBound" : BoundingType.THROUGH_ALL, "oppositeDirection" : true, "depth" : 25.4 * mm});
        }
        {
            var Q0;
            Q0=makeQuery(id+"F21.boolean.opBoolean","COPY",FACE,{"derivedFrom":makeQuery(id+"F21.opExtrude","SWEPT_FACE",FACE,{"disambiguationData":[OSD([sQuery(id+"F20.wireOp",EDGE,"E11.top")])]})});
            extrude(context, id + "F38", {"entities" : qUnion([Q0]), "operationType" : NewBodyOperationType.REMOVE, "oppositeDirection" : true, "depth" : 190.5 * mm});
        }
        {
            var Q0;
            Q0=makeQuery(id+"F21.boolean.opBoolean","COPY",FACE,{"derivedFrom":makeQuery(id+"F21.opExtrude","SWEPT_FACE",FACE,{"disambiguationData":[OSD([sQuery(id+"F20.wireOp",EDGE,"E11.bottom")])]})});
            extrude(context, id + "F39", {"entities" : qUnion([Q0]), "operationType" : NewBodyOperationType.ADD, "depth" : 190.5 * mm});
        }
        {
            var Q0;
            Q0=makeQuery(id+"F39.opExtrude","CAP_FACE",FACE,{"disambiguationData":[OSD([sQuery(id+"F20.wireOp",EDGE,"E11.bottom")])],"isStart":false});
            extrude(context, id + "F40", {"entities" : qUnion([Q0]), "operationType" : NewBodyOperationType.REMOVE, "oppositeDirection" : true, "depth" : 76.2 * mm});
        }
        {
            var Q0;
            {var subQ0=sQuery(id+"F16.wireOp",EDGE,"E9.right");Q0=makeQuery(id+"F18.boolean.opBoolean","MERGE",FACE,{"derivedFrom":[makeQuery(id+"F17.boolean.opBoolean","COPY",FACE,{"derivedFrom":makeQuery(id+"F17.opExtrude","SWEPT_FACE",FACE,{"disambiguationData":[OSD([subQ0])]})}),makeQuery(id+"F18.opExtrude","SWEPT_FACE",FACE,{"disambiguationData":[OSD([sQuery(id+"F16.wireOp",EDGE,"E9.bottom"),subQ0])]})]});}
            extrude(context, id + "F41", {"entities" : qUnion([Q0]), "operationType" : NewBodyOperationType.REMOVE, "oppositeDirection" : true, "depth" : 406.4 * mm});
        }
        {
            var Q0;
            {var subQ0=sQuery(id+"F16.wireOp",EDGE,"E9.left");Q0=makeQuery(id+"F18.boolean.opBoolean","MERGE",FACE,{"derivedFrom":[makeQuery(id+"F17.boolean.opBoolean","COPY",FACE,{"derivedFrom":makeQuery(id+"F17.opExtrude","SWEPT_FACE",FACE,{"disambiguationData":[OSD([subQ0])]})}),makeQuery(id+"F18.opExtrude","SWEPT_FACE",FACE,{"disambiguationData":[OSD([sQuery(id+"F16.wireOp",EDGE,"E9.bottom"),subQ0])]})]});}
            extrude(context, id + "F42", {"entities" : qUnion([Q0]), "operationType" : NewBodyOperationType.ADD, "depth" : 406.4 * mm});
        }
        {
            var Q0;
            {var subQ0=sQuery(id+"F22.wireOp",EDGE,"E13.left");Q0=makeQuery(id+"F37.boolean.opBoolean","MERGE",FACE,{"derivedFrom":[makeQuery(id+"F28.boolean.opBoolean","COPY",FACE,{"derivedFrom":makeQuery(id+"F28.opExtrude","CAP_FACE",FACE,{"disambiguationData":[OSD([subQ0])],"isStart":false})}),makeQuery(id+"F37.opExtrude","SWEPT_FACE",FACE,{"disambiguationData":[OSD([sQuery(id+"F22.wireOp",EDGE,"E13.bottom"),subQ0])]})]});}
            extrude(context, id + "F43", {"entities" : qUnion([Q0]), "operationType" : NewBodyOperationType.REMOVE, "oppositeDirection" : true, "depth" : 76.2 * mm});
        }
        {
            var Q0;
            {var subQ0=sQuery(id+"F22.wireOp",EDGE,"E13.right");Q0=makeQuery(id+"F37.boolean.opBoolean","MERGE",FACE,{"derivedFrom":[makeQuery(id+"F29.opExtrude","CAP_FACE",FACE,{"disambiguationData":[OSD([subQ0])],"isStart":false}),makeQuery(id+"F37.opExtrude","SWEPT_FACE",FACE,{"disambiguationData":[OSD([sQuery(id+"F22.wireOp",EDGE,"E13.bottom"),subQ0])]})]});}
            extrude(context, id + "F44", {"entities" : qUnion([Q0]), "operationType" : NewBodyOperationType.REMOVE, "oppositeDirection" : true, "depth" : 60.96 * mm});
        }
        {
            var Q0;
            Q0=makeQuery(id+"F38.boolean.opBoolean","COPY",FACE,{"derivedFrom":makeQuery(id+"F38.opExtrude","CAP_FACE",FACE,{"disambiguationData":[OSD([sQuery(id+"F20.wireOp",EDGE,"E11.top")])],"isStart":false})});
            extrude(context, id + "F45", {"entities" : qUnion([Q0]), "operationType" : NewBodyOperationType.ADD, "depth" : 25.4 * mm});
        }
        {
            var Q0;
            Q0=makeQuery(id+"F40.boolean.opBoolean","COPY",FACE,{"derivedFrom":makeQuery(id+"F40.opExtrude","CAP_FACE",FACE,{"disambiguationData":[OSD([sQuery(id+"F20.wireOp",EDGE,"E11.bottom")])],"isStart":false})});
            extrude(context, id + "F46", {"entities" : qUnion([Q0]), "operationType" : NewBodyOperationType.REMOVE, "oppositeDirection" : true, "depth" : 63.5 * mm});
        }
        {
            var Q0;
            {var subQ0=sQuery(id+"F32.wireOp",EDGE,"E17.bottom");var subQ1=sQuery(id+"F30.wireOp",EDGE,"E15.left");var subQ2=sQuery(id+"F2.wireOp",EDGE,"E4.right");var subQ3=sQuery(id+"F2.wireOp",EDGE,"E3.right");var subQ4=sQuery(id+"F2.wireOp",EDGE,"E3.bottom");var subQ5=sQuery(id+"F0.wireOp",EDGE,"E0.top");var subQ6=sQuery(id+"F0.wireOp",EDGE,"E0.right");var subQ7=sQuery(id+"F0.wireOp",EDGE,"E0.left");var subQ12=sQuery(id+"F2.wireOp",EDGE,"E4.bottom");var subQ13=sQuery(id+"F2.wireOp",EDGE,"E2.left");var subQ14=sQuery(id+"F2.wireOp",EDGE,"E2.top");var subQ16=sQuery(id+"F0.wireOp",EDGE,"E0.bottom");var subQ17=makeQuery(id+"F1.opExtrude","CAP_FACE",FACE,{"disambiguationData":[OSD([subQ16,subQ5,subQ7,subQ6])],"isStart":false});var subQ20=makeQuery(id+"F1.opExtrude","SWEPT_FACE",FACE,{"disambiguationData":[OSD([subQ16])]});var subQ21=makeQuery(id+"F15.boolean.opBoolean","MERGE",FACE,{"derivedFrom":[makeQuery(id+"F5.boolean.opBoolean","MERGE",FACE,{"derivedFrom":[makeQuery(id+"F4.boolean.opBoolean","MERGE",FACE,{"derivedFrom":[makeQuery(id+"F3.boolean.opBoolean","SPLIT",FACE,{"disambiguationData":[TD([subQ20])],"derivedFrom":subQ17}),makeQuery(id+"F4.opExtrude","SWEPT_FACE",FACE,{"disambiguationData":[OSD([subQ6]),TDD([makeQuery(id+"F3.boolean.opBoolean","SPLIT",EDGE,{"disambiguationData":[TD([subQ20])],"derivedFrom":makeQuery(id+"F1.opExtrude","CAP_EDGE",EDGE,{"disambiguationData":[OSD([subQ6])],"isStart":false})})])]})]}),makeQuery(id+"F5.opExtrude","SWEPT_FACE",FACE,{"disambiguationData":[OSD([subQ5])]})]}),makeQuery(id+"F15.opExtrude","SWEPT_FACE",FACE,{"disambiguationData":[OSD([subQ6,subQ14,subQ13,subQ12,subQ2]),TDD([makeQuery(id+"F13.boolean.opBoolean","MERGE",EDGE,{"derivedFrom":[makeQuery(id+"F4.boolean.opBoolean","MERGE",EDGE,{"derivedFrom":[makeQuery(id+"F3.opExtrude","CAP_EDGE",EDGE,{"disambiguationData":[OSD([subQ14,subQ12])],"isStart":true}),makeQuery(id+"F4.opExtrude","SWEPT_EDGE",EDGE,{"disambiguationData":[OSD([subQ6,subQ14,subQ13]),TDD([makeQuery(id+"F3.opExtrude","CAP_VERTEX",VERTEX,{"disambiguationData":[OSD([subQ6,subQ14,subQ13])],"isStart":true})])]})]}),makeQuery(id+"F13.opExtrude","SWEPT_EDGE",EDGE,{"disambiguationData":[OSD([subQ12,subQ2]),TDD([makeQuery(id+"F3.opExtrude","CAP_VERTEX",VERTEX,{"disambiguationData":[OSD([subQ12,subQ2])],"isStart":true})])]})]})])]})]});Q0=makeQuery(id+"F34.boolean.opBoolean","MERGE",FACE,{"derivedFrom":[makeQuery(id+"F33.boolean.opBoolean","MERGE",FACE,{"derivedFrom":[makeQuery(id+"F31.boolean.opBoolean","SPLIT",FACE,{"disambiguationData":[TD([subQ20])],"derivedFrom":subQ21}),makeQuery(id+"F31.boolean.opBoolean","SPLIT",FACE,{"disambiguationData":[TD([makeQuery(id+"F31.opExtrude","SWEPT_FACE",FACE,{"disambiguationData":[OSD([sQuery(id+"F30.wireOp",EDGE,"E15.right")])]})])],"derivedFrom":subQ21}),makeQuery(id+"F33.opExtrude","SWEPT_FACE",FACE,{"disambiguationData":[OSD([subQ0])]})]}),makeQuery(id+"F34.opExtrude","SWEPT_FACE",FACE,{"disambiguationData":[OSD([subQ5,subQ4,subQ3,subQ2,sQuery(id+"F30.wireOp",EDGE,"E15.top"),subQ1,subQ0,sQuery(id+"F32.wireOp",EDGE,"E17.right")])]})]});}
            var sketch = newSketch(context, id + "F47", { "sketchPlane" : qUnion([Q0])});
            skLineSegment(sketch, "E18.bottom", {"start": v(9909.97, 2408.24) * mm, "end": v(9489.95, 2408.24) * mm, "construction": true});
            skLineSegment(sketch, "E18.top", {"start": v(9909.97, 1704.46) * mm, "end": v(9489.95, 1704.46) * mm, "construction": true});
            skLineSegment(sketch, "E18.left", {"start": v(9909.97, 2408.24) * mm, "end": v(9909.97, 1704.46) * mm, "construction": true});
            skLineSegment(sketch, "E18.right", {"start": v(9489.95, 2408.24) * mm, "end": v(9489.95, 1704.46) * mm, "construction": true});
            skLineSegment(sketch, "E19.bottom", {"start": v(9489.95, 2408.24) * mm, "end": v(6060.95, 2408.24) * mm, "construction": true});
            skLineSegment(sketch, "E19.top", {"start": v(9489.95, 655.64) * mm, "end": v(6060.95, 655.64) * mm, "construction": true});
            skLineSegment(sketch, "E19.left", {"start": v(9489.95, 2408.24) * mm, "end": v(9489.95, 655.64) * mm, "construction": true});
            skLineSegment(sketch, "E19.right", {"start": v(6060.95, 2408.24) * mm, "end": v(6060.95, 655.64) * mm, "construction": true});
            skLineSegment(sketch, "E20.bottom", {"start": v(6060.95, 655.64) * mm, "end": v(5578.35, 655.64) * mm});
            skLineSegment(sketch, "E20.top", {"start": v(6060.95, 173.04) * mm, "end": v(5578.35, 173.04) * mm});
            skLineSegment(sketch, "E20.left", {"start": v(6060.95, 655.64) * mm, "end": v(6060.95, 173.04) * mm});
            skLineSegment(sketch, "E20.right", {"start": v(5578.35, 655.64) * mm, "end": v(5578.35, 173.04) * mm});
            skSolve(sketch);
        }
        {
            var Q0;
            Q0=makeQuery(id+"F47.imprint","IMPRINT",FACE,{"disambiguationData":[TD([[makeQuery(id+"F47.imprint","IMPRINT",EDGE,{"derivedFrom":sQuery(id+"F47.wireOp",EDGE,"E20.bottom")}),1.0]])]});
            var Q1;
            {var subQ0=sQuery(id+"F2.wireOp",EDGE,"E4.right");var subQ1=sQuery(id+"F2.wireOp",EDGE,"E3.right");var subQ2=sQuery(id+"F2.wireOp",EDGE,"E3.bottom");var subQ3=sQuery(id+"F0.wireOp",EDGE,"E0.top");var subQ4=sQuery(id+"F6.wireOp",EDGE,"E6.left");var subQ5=sQuery(id+"F6.wireOp",EDGE,"E6.top");var subQ6=sQuery(id+"F6.wireOp",EDGE,"E6.bottom");var subQ7=sQuery(id+"F6.wireOp",EDGE,"E5.right");var subQ8=sQuery(id+"F6.wireOp",EDGE,"E5.left");var subQ9=sQuery(id+"F6.wireOp",EDGE,"E5.top");var subQ10=sQuery(id+"F6.wireOp",EDGE,"E5.bottom");var subQ11=sQuery(id+"F2.wireOp",EDGE,"E4.bottom");var subQ12=sQuery(id+"F2.wireOp",EDGE,"E3.left");var subQ13=sQuery(id+"F2.wireOp",EDGE,"E2.left");var subQ14=sQuery(id+"F2.wireOp",EDGE,"E2.top");var subQ15=sQuery(id+"F2.wireOp",EDGE,"E2.bottom");Q1=makeQuery(id+"F31.boolean.opBoolean","MERGE",FACE,{"derivedFrom":[makeQuery(id+"F13.boolean.opBoolean","MERGE",FACE,{"derivedFrom":[makeQuery(id+"F11.boolean.opBoolean","MERGE",FACE,{"derivedFrom":[makeQuery(id+"F10.boolean.opBoolean","MERGE",FACE,{"derivedFrom":[makeQuery(id+"F8.boolean.opBoolean","MERGE",FACE,{"derivedFrom":[makeQuery(id+"F7.opExtrude","CAP_FACE",FACE,{"disambiguationData":[OSD([subQ10,subQ9,subQ8,subQ7,subQ6,subQ5,subQ4])],"isStart":false}),makeQuery(id+"F8.opExtrude","CAP_FACE",FACE,{"disambiguationData":[OSD([subQ15,subQ14,subQ13,subQ2,subQ12,subQ1,subQ11,subQ0])],"isStart":false})]}),makeQuery(id+"F10.opExtrude","CAP_FACE",FACE,{"disambiguationData":[OSD([subQ15,subQ14,subQ13,subQ2,subQ12,subQ1,subQ11,subQ0,subQ10,subQ9,subQ8,subQ7,subQ6,subQ5,subQ4])],"isStart":false})]}),makeQuery(id+"F11.opExtrude","SWEPT_FACE",FACE,{"disambiguationData":[OSD([subQ15,subQ14,subQ13,subQ2,subQ12,subQ1,subQ11,subQ0,subQ10,subQ9,subQ8,subQ7,subQ6,subQ5,subQ4,sQuery(id+"F9.wireOp",EDGE,"E7.top")])]})]}),makeQuery(id+"F13.opExtrude","SWEPT_FACE",FACE,{"disambiguationData":[OSD([subQ3,subQ2,subQ1,subQ0]),TDD([makeQuery(id+"F8.boolean.opBoolean","COPY",EDGE,{"derivedFrom":makeQuery(id+"F8.opExtrude","CAP_EDGE",EDGE,{"disambiguationData":[OSD([subQ3,subQ2,subQ1,subQ0])],"isStart":false})})])]})]}),makeQuery(id+"F31.opExtrude","SWEPT_FACE",FACE,{"disambiguationData":[OSD([sQuery(id+"F30.wireOp",EDGE,"E15.bottom")])]})]});}
            extrude(context, id + "F48", {"entities" : qUnion([Q0]), "operationType" : NewBodyOperationType.ADD, "endBound" : BoundingType.UP_TO_SURFACE, "endBoundEntityFace" : qUnion([Q1]), "depth" : 25.4 * mm});
        }
        {
            var Q0;
            {var subQ0=sQuery(id+"F6.wireOp",EDGE,"E5.left");var subQ1=sQuery(id+"F2.wireOp",EDGE,"E2.left");var subQ2=sQuery(id+"F0.wireOp",EDGE,"E0.right");var subQ3=sQuery(id+"F0.wireOp",EDGE,"E0.top");var subQ4=sQuery(id+"F22.wireOp",EDGE,"E13.right");var subQ5=sQuery(id+"F22.wireOp",EDGE,"E13.left");Q0=makeQuery(id+"F45.boolean.opBoolean","MERGE",FACE,{"derivedFrom":[makeQuery(id+"F39.boolean.opBoolean","MERGE",FACE,{"derivedFrom":[makeQuery(id+"F36.boolean.opBoolean","MERGE",FACE,{"derivedFrom":[makeQuery(id+"F29.boolean.opBoolean","MERGE",FACE,{"derivedFrom":[makeQuery(id+"F26.boolean.opBoolean","MERGE",FACE,{"derivedFrom":[makeQuery(id+"F25.boolean.opBoolean","MERGE",FACE,{"derivedFrom":[makeQuery(id+"F7.boolean.opBoolean","MERGE",FACE,{"derivedFrom":[makeQuery(id+"F5.boolean.opBoolean","MERGE",FACE,{"derivedFrom":[makeQuery(id+"F4.opExtrude","CAP_FACE",FACE,{"disambiguationData":[OSD([subQ2,subQ1])],"isStart":false}),makeQuery(id+"F5.opExtrude","SWEPT_FACE",FACE,{"disambiguationData":[OSD([subQ3,subQ2]),TDD([makeQuery(id+"F4.opExtrude","CAP_EDGE",EDGE,{"disambiguationData":[OSD([subQ3,subQ2])],"isStart":false})])]})]}),makeQuery(id+"F7.opExtrude","SWEPT_FACE",FACE,{"disambiguationData":[OSD([subQ0])]})]}),makeQuery(id+"F25.opExtrude","SWEPT_FACE",FACE,{"disambiguationData":[OSD([subQ3,subQ2,subQ1,subQ0,subQ5])]})]}),makeQuery(id+"F26.opExtrude","SWEPT_FACE",FACE,{"disambiguationData":[OSD([subQ3,subQ2,subQ1,subQ0,subQ4])]})]}),makeQuery(id+"F29.opExtrude","SWEPT_FACE",FACE,{"disambiguationData":[OSD([subQ3,subQ2,subQ1,subQ0,subQ4])]})]}),makeQuery(id+"F36.opExtrude","SWEPT_FACE",FACE,{"disambiguationData":[OSD([subQ3,subQ2,subQ1,subQ0,sQuery(id+"F22.wireOp",EDGE,"E13.top"),subQ5,subQ4])]})]}),makeQuery(id+"F39.opExtrude","SWEPT_FACE",FACE,{"disambiguationData":[OSD([subQ3,subQ2,subQ1,subQ0,sQuery(id+"F20.wireOp",EDGE,"E11.bottom")])]})]}),makeQuery(id+"F45.opExtrude","SWEPT_FACE",FACE,{"disambiguationData":[OSD([subQ3,subQ2,subQ1,subQ0,sQuery(id+"F20.wireOp",EDGE,"E11.top")])]})]});}
            extrude(context, id + "F49", {"entities" : qUnion([Q0]), "operationType" : NewBodyOperationType.REMOVE, "oppositeDirection" : true, "depth" : 20.07 * mm, "offsetDistance" : 25.4 * mm});
        }
        {
            var Q0;
            Q0=makeQuery(id+"F49.boolean.opBoolean","COPY",FACE,{"derivedFrom":makeQuery(id+"F49.opExtrude","CAP_FACE",FACE,{"disambiguationData":[OSD([sQuery(id+"F0.wireOp",EDGE,"E0.top"),sQuery(id+"F0.wireOp",EDGE,"E0.right"),sQuery(id+"F2.wireOp",EDGE,"E2.left"),sQuery(id+"F6.wireOp",EDGE,"E5.left"),sQuery(id+"F20.wireOp",EDGE,"E11.bottom"),sQuery(id+"F20.wireOp",EDGE,"E11.top"),sQuery(id+"F22.wireOp",EDGE,"E13.top"),sQuery(id+"F22.wireOp",EDGE,"E13.left"),sQuery(id+"F22.wireOp",EDGE,"E13.right")])],"isStart":false})});
            extrude(context, id + "F50", {"entities" : qUnion([Q0]), "operationType" : NewBodyOperationType.REMOVE, "oppositeDirection" : true, "depth" : 12.7 * mm, "offsetDistance" : 25.4 * mm});
        }
        {
            var Q0;
            Q0=makeQuery(id+"F50.boolean.opBoolean","COPY",FACE,{"derivedFrom":makeQuery(id+"F50.opExtrude","CAP_FACE",FACE,{"disambiguationData":[OSD([sQuery(id+"F0.wireOp",EDGE,"E0.top"),sQuery(id+"F0.wireOp",EDGE,"E0.right"),sQuery(id+"F2.wireOp",EDGE,"E2.left"),sQuery(id+"F6.wireOp",EDGE,"E5.left"),sQuery(id+"F20.wireOp",EDGE,"E11.bottom"),sQuery(id+"F20.wireOp",EDGE,"E11.top"),sQuery(id+"F22.wireOp",EDGE,"E13.top"),sQuery(id+"F22.wireOp",EDGE,"E13.left"),sQuery(id+"F22.wireOp",EDGE,"E13.right")])],"isStart":false})});
            extrude(context, id + "F51", {"entities" : qUnion([Q0]), "operationType" : NewBodyOperationType.ADD, "depth" : 11.33 * mm, "offsetDistance" : 25.4 * mm});
        }
    });
